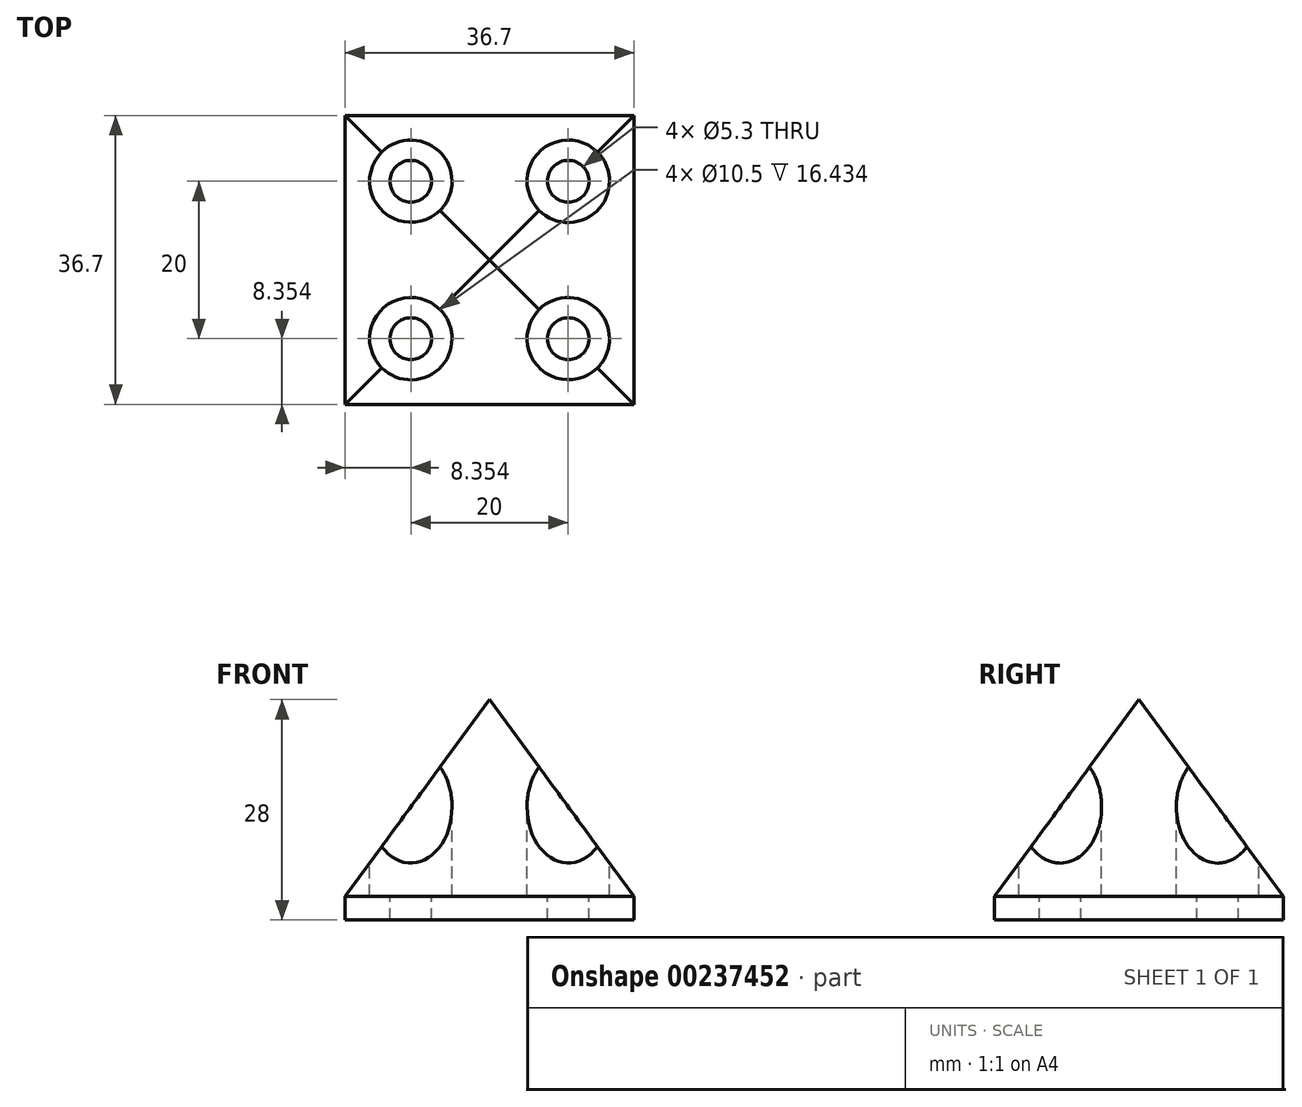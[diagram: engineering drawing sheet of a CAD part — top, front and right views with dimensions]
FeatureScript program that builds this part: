
annotation { "Feature Type Name" : "Feature", "Feature Type Description" : "" }
export const myFeature = defineFeature(function(context is Context, id is Id, definition is map)
    precondition{}
    {
        {
            var Q0;
            Q0=qCreatedBy(makeId("Top.planeOp"),FACE);
            var sketch = newSketch(context, id + "F0", { "sketchPlane" : qUnion([Q0])});
            skLineSegment(sketch, "E0.bottom", {"start": v(-20.96, -9.96) * mm, "end": v(15.74, -9.96) * mm});
            skLineSegment(sketch, "E0.top", {"start": v(-20.96, -46.66) * mm, "end": v(15.74, -46.66) * mm});
            skLineSegment(sketch, "E0.left", {"start": v(-20.96, -9.96) * mm, "end": v(-20.96, -46.66) * mm});
            skLineSegment(sketch, "E0.right", {"start": v(15.74, -9.96) * mm, "end": v(15.74, -46.66) * mm});
            skCircle(sketch, "E1", {"center": v(7.4, -18.3) * mm, "radius": 2.65 * mm});
            skCircle(sketch, "E2", {"center": v(-12.6, -18.3) * mm, "radius": 2.65 * mm});
            skCircle(sketch, "E3", {"center": v(7.4, -38.3) * mm, "radius": 2.65 * mm});
            skCircle(sketch, "E4", {"center": v(-12.6, -38.3) * mm, "radius": 2.65 * mm});
            skCircle(sketch, "E5", {"center": v(-12.6, -18.3) * mm, "radius": 5.25 * mm});
            skCircle(sketch, "E6", {"center": v(-12.6, -38.3) * mm, "radius": 5.25 * mm});
            skCircle(sketch, "E7", {"center": v(7.4, -38.3) * mm, "radius": 5.25 * mm});
            skCircle(sketch, "E8", {"center": v(7.4, -18.3) * mm, "radius": 5.25 * mm});
            skSolve(sketch);
        }
        {
            var Q0;
            Q0=makeQuery(id+"F0.imprint","IMPRINT",FACE,{"disambiguationData":[TD([[makeQuery(id+"F0.imprint","IMPRINT",EDGE,{"derivedFrom":sQuery(id+"F0.wireOp",EDGE,"E0.bottom")}),-1.0]])]});
            var Q1;
            Q1=makeQuery(id+"F0.imprint","IMPRINT",FACE,{"disambiguationData":[TD([[makeQuery(id+"F0.imprint","IMPRINT",EDGE,{"derivedFrom":sQuery(id+"F0.wireOp",EDGE,"E4")}),-1.0]])]});
            var Q2;
            Q2=makeQuery(id+"F0.imprint","IMPRINT",FACE,{"disambiguationData":[TD([[makeQuery(id+"F0.imprint","IMPRINT",EDGE,{"derivedFrom":sQuery(id+"F0.wireOp",EDGE,"E4")}),1.0]])]});
            var Q3;
            Q3=makeQuery(id+"F0.imprint","IMPRINT",FACE,{"disambiguationData":[TD([[makeQuery(id+"F0.imprint","IMPRINT",EDGE,{"derivedFrom":sQuery(id+"F0.wireOp",EDGE,"E3")}),-1.0]])]});
            var Q4;
            Q4=makeQuery(id+"F0.imprint","IMPRINT",FACE,{"disambiguationData":[TD([[makeQuery(id+"F0.imprint","IMPRINT",EDGE,{"derivedFrom":sQuery(id+"F0.wireOp",EDGE,"E3")}),1.0]])]});
            var Q5;
            Q5=makeQuery(id+"F0.imprint","IMPRINT",FACE,{"disambiguationData":[TD([[makeQuery(id+"F0.imprint","IMPRINT",EDGE,{"derivedFrom":sQuery(id+"F0.wireOp",EDGE,"E1")}),-1.0]])]});
            var Q6;
            Q6=makeQuery(id+"F0.imprint","IMPRINT",FACE,{"disambiguationData":[TD([[makeQuery(id+"F0.imprint","IMPRINT",EDGE,{"derivedFrom":sQuery(id+"F0.wireOp",EDGE,"E1")}),1.0]])]});
            var Q7;
            Q7=makeQuery(id+"F0.imprint","IMPRINT",FACE,{"disambiguationData":[TD([[makeQuery(id+"F0.imprint","IMPRINT",EDGE,{"derivedFrom":sQuery(id+"F0.wireOp",EDGE,"E2")}),-1.0]])]});
            var Q8;
            Q8=makeQuery(id+"F0.imprint","IMPRINT",FACE,{"disambiguationData":[TD([[makeQuery(id+"F0.imprint","IMPRINT",EDGE,{"derivedFrom":sQuery(id+"F0.wireOp",EDGE,"E2")}),1.0]])]});
            extrude(context, id + "F1", {"entities" : qUnion([Q0, Q1, Q2, Q3, Q4, Q5, Q6, Q7, Q8]), "depth" : 25 * mm});
        }
        {
            var Q0;
            Q0=makeQuery(id+"F1.opExtrude","SWEPT_FACE",FACE,{"disambiguationData":[OSD([sQuery(id+"F0.wireOp",EDGE,"E0.top")])]});
            var sketch = newSketch(context, id + "F2", { "sketchPlane" : qUnion([Q0])});
            skPoint(sketch, "E9", {"position": v(-2.6, 25) * mm});
            skLineSegment(sketch, "E10", {"start": v(-2.6, 25) * mm, "end": v(15.74, 0) * mm});
            skLineSegment(sketch, "E11", {"start": v(-2.6, 25) * mm, "end": v(-20.96, 0) * mm});
            skSolve(sketch);
        }
        {
            var Q0;
            {var subQ0=sQuery(id+"F2.wireOp",EDGE,"E11");Q0=makeQuery(id+"F2.imprint","IMPRINT",FACE,{"disambiguationData":[TD([[makeQuery(id+"F2.imprint","IMPRINT",EDGE,{"derivedFrom":subQ0}),-1.0]])]});}
            var Q1;
            {var subQ0=sQuery(id+"F2.wireOp",EDGE,"E10");Q1=makeQuery(id+"F2.imprint","IMPRINT",FACE,{"disambiguationData":[TD([[makeQuery(id+"F2.imprint","IMPRINT",EDGE,{"derivedFrom":subQ0}),1.0]])]});}
            extrude(context, id + "F3", {"entities" : qUnion([Q0, Q1]), "operationType" : NewBodyOperationType.REMOVE, "endBound" : BoundingType.THROUGH_ALL, "oppositeDirection" : true, "depth" : 25 * mm});
        }
        {
            var Q0;
            Q0=qCreatedBy(makeId("Right.planeOp"),FACE);
            var sketch = newSketch(context, id + "F4", { "sketchPlane" : qUnion([Q0])});
            skPoint(sketch, "E12", {"position": v(-28.3, 25) * mm});
            skLineSegment(sketch, "E13", {"start": v(-28.3, 25) * mm, "end": v(-46.66, 0) * mm});
            skLineSegment(sketch, "E14", {"start": v(-46.66, 0) * mm, "end": v(-46.66, 25) * mm});
            skLineSegment(sketch, "E15", {"start": v(-46.66, 25) * mm, "end": v(-28.3, 25) * mm});
            skLineSegment(sketch, "E16", {"start": v(-28.3, 25) * mm, "end": v(-9.96, 25) * mm});
            skLineSegment(sketch, "E17", {"start": v(-9.96, 25) * mm, "end": v(-9.96, 0) * mm});
            skLineSegment(sketch, "E18", {"start": v(-9.96, 0) * mm, "end": v(-28.3, 25) * mm});
            skSolve(sketch);
        }
        {
            var Q0;
            Q0=qSketchRegion(id+"F4",true);
            extrude(context, id + "F5", {"entities" : qUnion([Q0]), "operationType" : NewBodyOperationType.REMOVE, "oppositeDirection" : true, "depth" : 86.4 * mm, "symmetric" : true});
        }
        {
            var Q0;
            Q0=makeQuery(id+"F1.opExtrude","CAP_FACE",FACE,{"disambiguationData":[OSD([sQuery(id+"F0.wireOp",EDGE,"E0.bottom"),sQuery(id+"F0.wireOp",EDGE,"E0.top"),sQuery(id+"F0.wireOp",EDGE,"E0.left"),sQuery(id+"F0.wireOp",EDGE,"E0.right")])],"isStart":true});
            extrude(context, id + "F6", {"entities" : qUnion([Q0]), "operationType" : NewBodyOperationType.ADD, "depth" : 3 * mm});
        }
        {
            var Q0;
            Q0=qCreatedBy(makeId("Top.planeOp"),FACE);
            cPlane(context, id + "F7", {"entities" : qUnion([Q0]), "cplaneType" : CPlaneType.OFFSET, "offset" : 50 * mm, "width" : 150 * mm, "height" : 150 * mm});
        }
        {
            var Q0;
            Q0=qCreatedBy(id+"F7.planeOp",FACE);
            var sketch = newSketch(context, id + "F8", { "sketchPlane" : qUnion([Q0])});
            skPoint(sketch, "E19.0", {"position": v(7.4, -38.3) * mm});
            skPoint(sketch, "E20.0", {"position": v(7.4, -18.3) * mm});
            skPoint(sketch, "E21.0", {"position": v(-12.6, -18.3) * mm});
            skPoint(sketch, "E22.0", {"position": v(-12.6, -38.3) * mm});
            skSolve(sketch);
        }
        {
            var Q0;
            Q0=sQuery(id+"F8.wireOp",VERTEX,"E22.0");
            var Q1;
            Q1=sQuery(id+"F8.wireOp",VERTEX,"E21.0");
            var Q2;
            Q2=sQuery(id+"F8.wireOp",VERTEX,"E20.0");
            var Q3;
            Q3=sQuery(id+"F8.wireOp",VERTEX,"E19.0");
            var Q4;
            Q4=makeQuery(id+"F1.opExtrude","SWEPT_BODY",BODY,{"disambiguationData":[OSD([sQuery(id+"F0.wireOp",EDGE,"E0.bottom"),sQuery(id+"F0.wireOp",EDGE,"E0.top"),sQuery(id+"F0.wireOp",EDGE,"E0.left"),sQuery(id+"F0.wireOp",EDGE,"E0.right")])]});
            hole(context, id + "F9", {"style" : HoleStyle.C_BORE, "endStyle" : HoleEndStyle.BLIND, "holeDiameter" : 5.3 * mm, "cBoreDiameter" : 10.5 * mm, "cBoreDepth" : 50 * mm, "holeDepth" : 55 * mm, "startFromSketch" : true, "locations" : qUnion([Q0, Q1, Q2, Q3]), "scope" : qUnion([Q4])});
        }
    });
